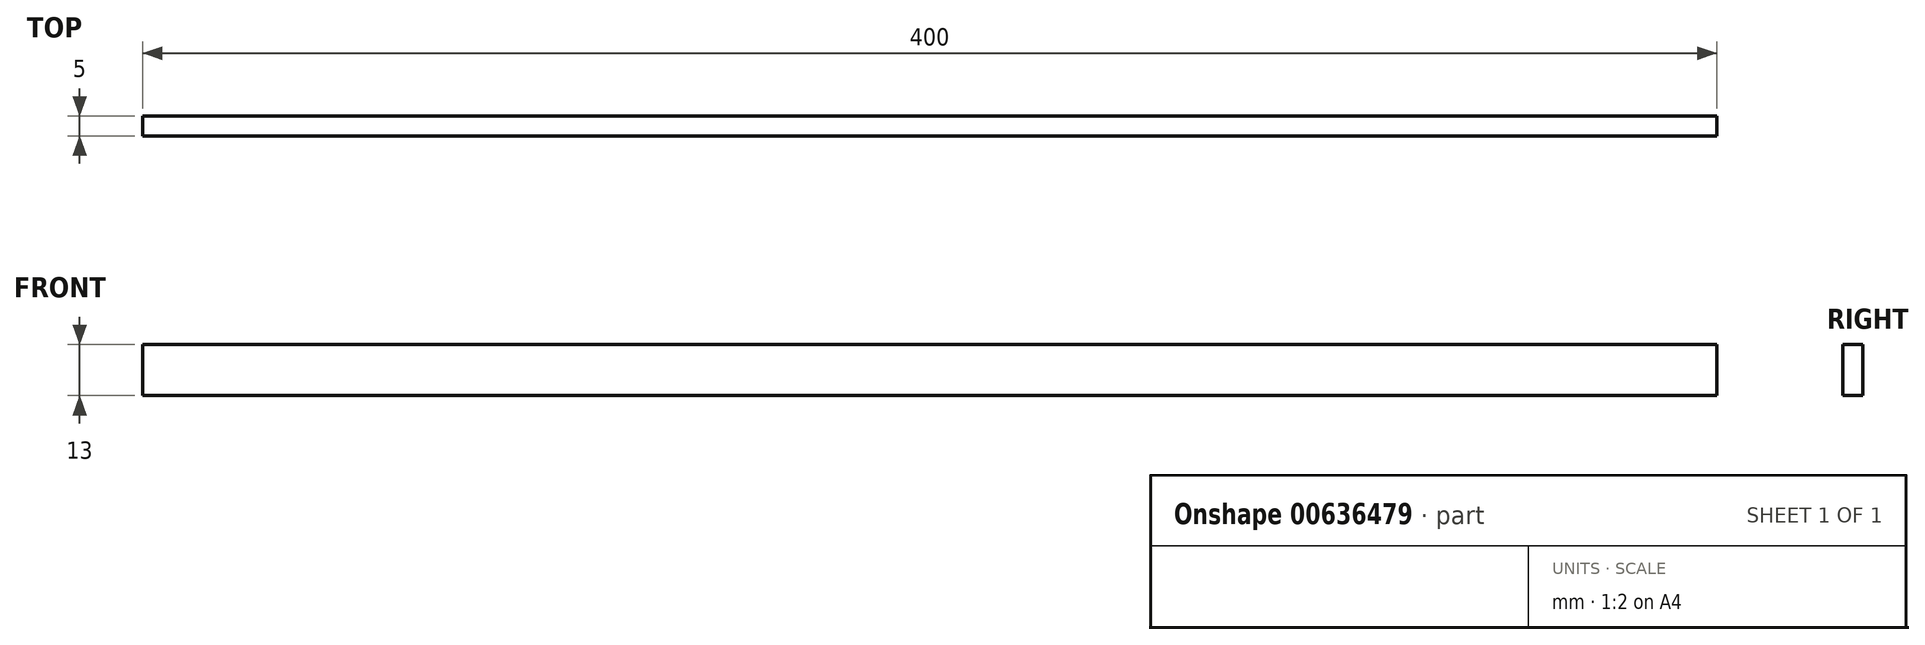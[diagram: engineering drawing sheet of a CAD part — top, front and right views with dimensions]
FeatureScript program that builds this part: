
annotation { "Feature Type Name" : "Feature", "Feature Type Description" : "" }
export const myFeature = defineFeature(function(context is Context, id is Id, definition is map)
    precondition{}
    {
        {
            var Q0;
            Q0=qCreatedBy(makeId("Top.planeOp"),FACE);
            var sketch = newSketch(context, id + "F0", { "sketchPlane" : qUnion([Q0])});
            skLineSegment(sketch, "E0.top", {"start": v(-200, 5) * mm, "end": v(200, 5) * mm});
            skLineSegment(sketch, "E0.left", {"start": v(-200, 0) * mm, "end": v(-200, 5) * mm});
            skLineSegment(sketch, "E0.right", {"start": v(200, 0) * mm, "end": v(200, 5) * mm});
            skLineSegment(sketch, "E1", {"start": v(-200, 0) * mm, "end": v(200, 0) * mm});
            skSolve(sketch);
        }
        {
            var Q0;
            Q0=makeQuery(id+"F0.imprint","IMPRINT",FACE,{"disambiguationData":[TD([[makeQuery(id+"F0.imprint","IMPRINT",EDGE,{"derivedFrom":sQuery(id+"F0.wireOp",EDGE,"E0.top")}),-1.0]])]});
            extrude(context, id + "F1", {"entities" : qUnion([Q0]), "depth" : 13 * mm, "offsetDistance" : 25 * mm});
        }
    });
